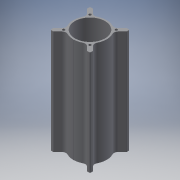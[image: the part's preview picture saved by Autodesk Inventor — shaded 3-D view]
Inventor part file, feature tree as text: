
AUTODESK INVENTOR PART (.ipt)
format: ipt  version: 2016 (Build 200138000, 138)  size: 148,480 bytes
history: native  units: mm
features: extrude x1, sketch x1
ambient origin geometry x8: Origin, YZ Plane, XZ Plane, XY Plane, X Axis, Y Axis, Z Axis, Center Point
bodies: Solid1 (feature_tree)
feature tree (2):
  extrude  "Extrusion1"  [1 undecoded]
  sketch  "Sketch1"  dims[d0=250.0mm d1=0.0mm]
note: 1 required parameter value undecoded (feature->parameter linkage not recoverable at this tier; creation-order binding heuristic only, values carry confidence <= 0.55)
